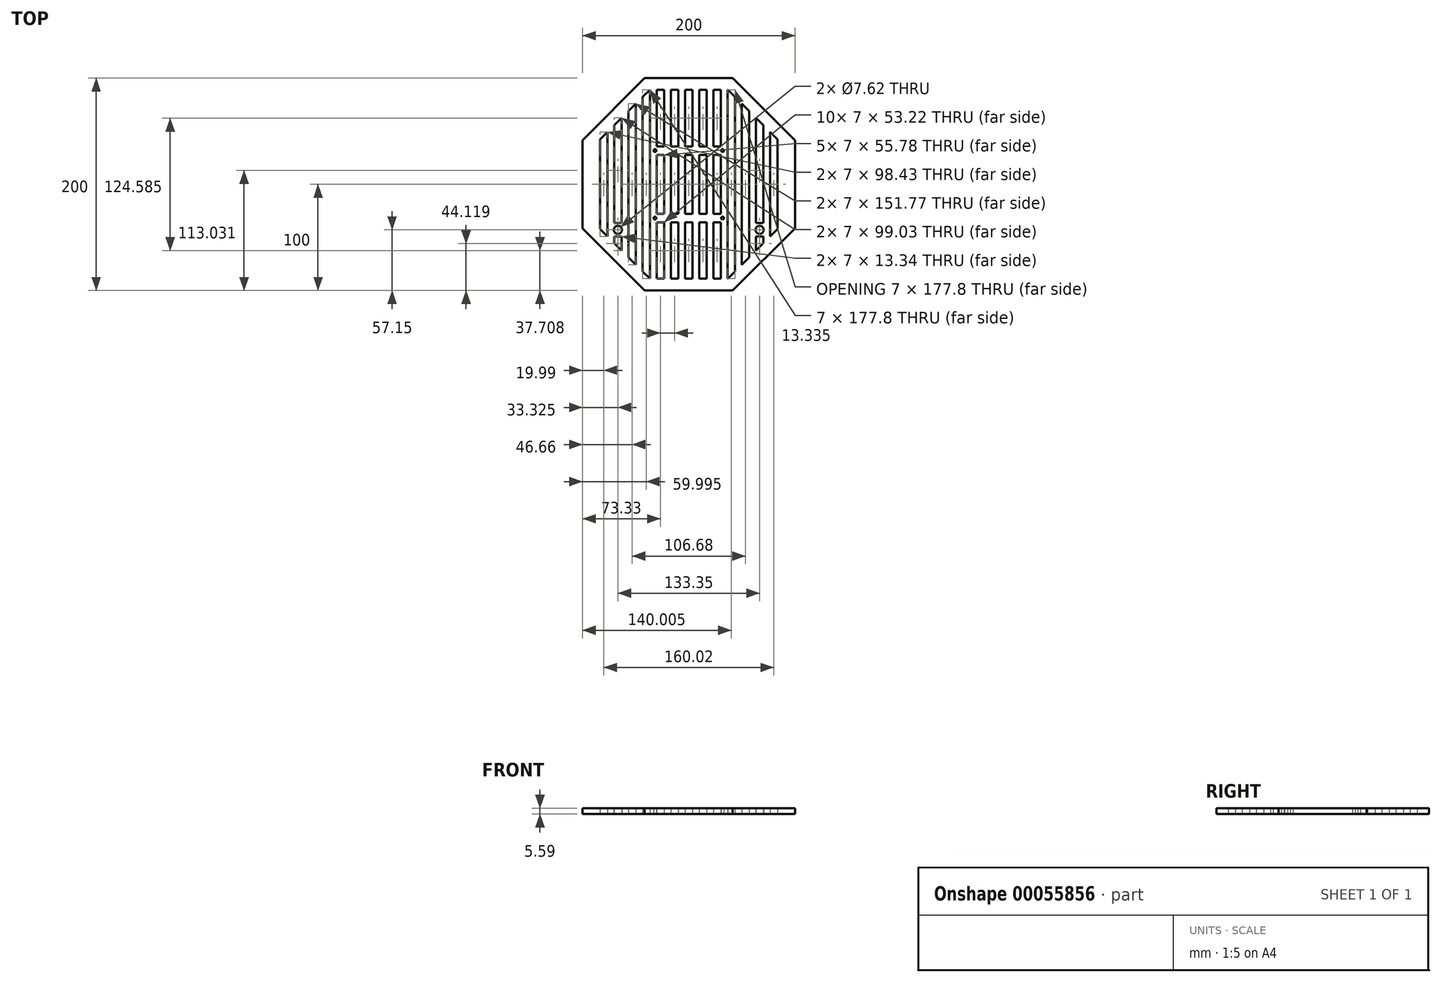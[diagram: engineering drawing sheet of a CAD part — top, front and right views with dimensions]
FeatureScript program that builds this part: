
annotation { "Feature Type Name" : "Feature", "Feature Type Description" : "" }
export const myFeature = defineFeature(function(context is Context, id is Id, definition is map)
    precondition{}
    {
        {
            var Q0;
            Q0=qCreatedBy(makeId("Top.planeOp"),FACE);
            var sketch = newSketch(context, id + "F0", { "sketchPlane" : qUnion([Q0])});
            skLineSegment(sketch, "E0.0", {"start": v(-41.42, 100) * mm, "end": v(41.42, 100) * mm});
            skLineSegment(sketch, "E0.2", {"start": v(100, 41.42) * mm, "end": v(100, -41.42) * mm});
            skLineSegment(sketch, "E0.3", {"start": v(100, -41.42) * mm, "end": v(41.42, -100) * mm});
            skLineSegment(sketch, "E0.4", {"start": v(41.42, -100) * mm, "end": v(-41.42, -100) * mm});
            skLineSegment(sketch, "E0.5", {"start": v(-41.42, -100) * mm, "end": v(-100, -41.42) * mm});
            skLineSegment(sketch, "E0.6", {"start": v(-100, -41.42) * mm, "end": v(-100, 41.42) * mm});
            skLineSegment(sketch, "E0.7", {"start": v(-100, 41.42) * mm, "end": v(-41.42, 100) * mm});
            skPoint(sketch, "E0.0.midPoint", {"position": v(0, 100) * mm});
            skPoint(sketch, "E1.rect.middle", {"position": v(0, 0) * mm});
            skCircle(sketch, "E2", {"center": v(-31.79, 31.79) * mm, "radius": 1.3 * mm});
            skCircle(sketch, "E3", {"center": v(31.79, 31.79) * mm, "radius": 1.3 * mm});
            skCircle(sketch, "E4", {"center": v(-31.79, -31.79) * mm, "radius": 1.3 * mm});
            skCircle(sketch, "E5", {"center": v(31.79, -31.79) * mm, "radius": 1.3 * mm});
            skPoint(sketch, "E6", {"position": v(0, -42.85) * mm});
            skCircle(sketch, "E7", {"center": v(-66.68, -42.85) * mm, "radius": 3.81 * mm});
            skCircle(sketch, "E8", {"center": v(66.68, -42.85) * mm, "radius": 3.81 * mm});
            skPoint(sketch, "E9.0.midPoint", {"position": v(0, 88.9) * mm});
            skLineSegment(sketch, "E10.bottom", {"start": v(-3.5, 88.9) * mm, "end": v(3.5, 88.9) * mm});
            skLineSegment(sketch, "E10.top", {"start": v(-3.5, -88.9) * mm, "end": v(3.5, -88.9) * mm});
            skLineSegment(sketch, "E10.left", {"start": v(-3.5, 88.9) * mm, "end": v(-3.5, 35.68) * mm});
            skLineSegment(sketch, "E10.right", {"start": v(3.5, 88.9) * mm, "end": v(3.5, 35.68) * mm});
            skLineSegment(sketch, "E11.1.0.0", {"start": v(9.84, 88.9) * mm, "end": v(9.84, 35.68) * mm});
            skLineSegment(sketch, "E11.1.0.1", {"start": v(16.84, 88.9) * mm, "end": v(16.84, 35.68) * mm});
            skPoint(sketch, "E11.1.0.2", {"position": v(13.33, -42.85) * mm});
            skPoint(sketch, "E11.1.0.3", {"position": v(13.33, 0) * mm});
            skPoint(sketch, "E11.1.0.4", {"position": v(13.33, 88.9) * mm});
            skPoint(sketch, "E11.1.0.5", {"position": v(13.33, 0) * mm});
            skLineSegment(sketch, "E11.1.0.6", {"start": v(9.84, 88.9) * mm, "end": v(16.84, 88.9) * mm});
            skLineSegment(sketch, "E11.1.0.7", {"start": v(9.84, -88.9) * mm, "end": v(16.84, -88.9) * mm});
            skLineSegment(sketch, "E11.2.0.0", {"start": v(23.17, 88.9) * mm, "end": v(23.17, 35.68) * mm});
            skLineSegment(sketch, "E11.2.0.1", {"start": v(30.17, 88.9) * mm, "end": v(30.17, 35.68) * mm});
            skPoint(sketch, "E11.2.0.2", {"position": v(26.67, -42.85) * mm});
            skPoint(sketch, "E11.2.0.3", {"position": v(26.67, 0) * mm});
            skPoint(sketch, "E11.2.0.4", {"position": v(26.67, 88.9) * mm});
            skPoint(sketch, "E11.2.0.5", {"position": v(26.67, 0) * mm});
            skLineSegment(sketch, "E11.2.0.6", {"start": v(23.17, 88.9) * mm, "end": v(30.17, 88.9) * mm});
            skLineSegment(sketch, "E11.2.0.7", {"start": v(23.17, -88.9) * mm, "end": v(30.17, -88.9) * mm});
            skLineSegment(sketch, "E11.3.0.0", {"start": v(36.5, 88.9) * mm, "end": v(36.5, -88.9) * mm});
            skLineSegment(sketch, "E11.3.0.1", {"start": v(43.5, 82.22) * mm, "end": v(43.5, -82.22) * mm});
            skPoint(sketch, "E11.3.0.2", {"position": v(40, -42.85) * mm});
            skPoint(sketch, "E11.3.0.3", {"position": v(40, 0) * mm});
            skPoint(sketch, "E11.3.0.5", {"position": v(40, 0) * mm});
            skLineSegment(sketch, "E11.3.0.6", {"start": v(36.5, 88.9) * mm, "end": v(36.82, 88.9) * mm});
            skLineSegment(sketch, "E11.3.0.7", {"start": v(36.5, -88.9) * mm, "end": v(36.82, -88.9) * mm});
            skPoint(sketch, "E11.4.0.2", {"position": v(53.34, -42.85) * mm});
            skPoint(sketch, "E11.4.0.3", {"position": v(53.34, 0) * mm});
            skPoint(sketch, "E11.4.0.5", {"position": v(53.34, 0) * mm});
            skPoint(sketch, "E11.5.0.2", {"position": v(66.67, -42.85) * mm});
            skPoint(sketch, "E11.5.0.3", {"position": v(66.67, 0) * mm});
            skPoint(sketch, "E11.5.0.5", {"position": v(66.67, 0) * mm});
            skLineSegment(sketch, "E11.6.0.1", {"start": v(83.51, 42.21) * mm, "end": v(83.51, -42.21) * mm});
            skPoint(sketch, "E11.6.0.2", {"position": v(80, -42.85) * mm});
            skPoint(sketch, "E11.6.0.3", {"position": v(80, 0) * mm});
            skPoint(sketch, "E11.6.0.5", {"position": v(80, 0) * mm});
            skLineSegment(sketch, "E11.direction1", {"start": v(-3.5, -88.9) * mm, "end": v(9.84, -88.9) * mm, "construction": true});
            skLineSegment(sketch, "E12", {"start": v(0, 88.9) * mm, "end": v(0, -110.43) * mm, "construction": true});
            skPoint(sketch, "E12.endSnap0", {"position": v(0, -100) * mm});
            skLineSegment(sketch, "E13.MirrorCS", {"start": v(-36.5, 88.9) * mm, "end": v(-36.82, 88.9) * mm});
            skLineSegment(sketch, "E14.MirrorCS", {"start": v(-9.84, 88.9) * mm, "end": v(-16.84, 88.9) * mm});
            skLineSegment(sketch, "E15.MirrorCS", {"start": v(-23.17, -88.9) * mm, "end": v(-30.17, -88.9) * mm});
            skLineSegment(sketch, "E16.MirrorCS", {"start": v(-23.17, 88.9) * mm, "end": v(-30.17, 88.9) * mm});
            skLineSegment(sketch, "E17.MirrorCS", {"start": v(-36.5, -88.9) * mm, "end": v(-36.82, -88.9) * mm});
            skLineSegment(sketch, "E18.MirrorCS", {"start": v(-9.83, -88.9) * mm, "end": v(-16.83, -88.9) * mm});
            skPoint(sketch, "E19.MirrorP", {"position": v(-66.67, 0) * mm});
            skPoint(sketch, "E20.MirrorP", {"position": v(-53.34, 0) * mm});
            skPoint(sketch, "E21.MirrorP", {"position": v(-40, 0) * mm});
            skPoint(sketch, "E22.MirrorP", {"position": v(-26.67, 0) * mm});
            skPoint(sketch, "E23.MirrorP", {"position": v(-13.33, 0) * mm});
            skArc(sketch, "E24.MirrorC", {"start": v(-63.17, -44.36) * mm, "mid": v(-70.48, -42.85) * mm, "end": v(-63.17, -41.34) * mm});
            skPoint(sketch, "E25.MirrorP", {"position": v(-80, 0) * mm});
            skLineSegment(sketch, "E26.MirrorCS", {"start": v(-30.17, 88.9) * mm, "end": v(-30.17, 35.68) * mm});
            skPoint(sketch, "E27.MirrorP", {"position": v(-26.67, -42.85) * mm});
            skPoint(sketch, "E28.MirrorP", {"position": v(-40, -42.85) * mm});
            skLineSegment(sketch, "E29.MirrorCS", {"start": v(-16.84, 88.9) * mm, "end": v(-16.83, 35.68) * mm});
            skPoint(sketch, "E30.MirrorP", {"position": v(-53.34, -42.85) * mm});
            skPoint(sketch, "E31.MirrorP", {"position": v(-13.33, 88.9) * mm});
            skLineSegment(sketch, "E32.MirrorCS", {"start": v(-36.5, 88.9) * mm, "end": v(-36.5, -88.9) * mm});
            skLineSegment(sketch, "E33.MirrorCS", {"start": v(-43.5, 82.22) * mm, "end": v(-43.5, -82.22) * mm});
            skPoint(sketch, "E34.MirrorP", {"position": v(-13.33, -42.85) * mm});
            skLineSegment(sketch, "E35.MirrorCS", {"start": v(-9.84, 88.9) * mm, "end": v(-9.83, 35.68) * mm});
            skPoint(sketch, "E36.MirrorP", {"position": v(-66.67, -42.85) * mm});
            skPoint(sketch, "E37.MirrorP", {"position": v(-26.67, 88.9) * mm});
            skLineSegment(sketch, "E38.MirrorCS", {"start": v(-23.17, 88.9) * mm, "end": v(-23.17, 35.68) * mm});
            skPoint(sketch, "E39.MirrorP", {"position": v(-80, -42.85) * mm});
            skLineSegment(sketch, "E40.trimOffspring", {"start": v(-83.5, 42.21) * mm, "end": v(-83.5, -42.21) * mm});
            skLineSegment(sketch, "E41.trimOffspring", {"start": v(-76.5, 49.21) * mm, "end": v(-76.5, -49.21) * mm});
            skLineSegment(sketch, "E42.trimOffspring", {"start": v(-70.17, 55.55) * mm, "end": v(-70.17, -36.49) * mm});
            skLineSegment(sketch, "E43.trimOffspring", {"start": v(-63.17, 62.55) * mm, "end": v(-63.17, -36.49) * mm});
            skLineSegment(sketch, "E44.trimOffspring", {"start": v(-56.84, 68.88) * mm, "end": v(-56.84, -68.88) * mm});
            skLineSegment(sketch, "E45.trimOffspring", {"start": v(-49.84, 75.88) * mm, "end": v(-49.84, -75.88) * mm});
            skLineSegment(sketch, "E46.trimOffspring", {"start": v(49.84, 75.88) * mm, "end": v(49.84, -75.88) * mm});
            skLineSegment(sketch, "E47.trimOffspring", {"start": v(56.84, 68.88) * mm, "end": v(56.84, -68.88) * mm});
            skLineSegment(sketch, "E48.trimOffspring", {"start": v(63.17, 62.55) * mm, "end": v(63.17, -36.49) * mm});
            skLineSegment(sketch, "E49.trimOffspring", {"start": v(76.5, 49.21) * mm, "end": v(76.5, -49.21) * mm});
            skLineSegment(sketch, "E50", {"start": v(41.42, 100) * mm, "end": v(100, 41.42) * mm});
            skLineSegment(sketch, "E51", {"start": v(-36.5, -88.9) * mm, "end": v(-43.5, -82.22) * mm});
            skLineSegment(sketch, "E52", {"start": v(-49.84, -75.88) * mm, "end": v(-56.84, -68.88) * mm});
            skLineSegment(sketch, "E53", {"start": v(-63.17, -62.55) * mm, "end": v(-70.17, -55.55) * mm});
            skLineSegment(sketch, "E54", {"start": v(-76.5, -49.21) * mm, "end": v(-83.5, -42.21) * mm});
            skLineSegment(sketch, "E55", {"start": v(36.82, -88.9) * mm, "end": v(43.5, -82.22) * mm});
            skLineSegment(sketch, "E56", {"start": v(49.84, -75.88) * mm, "end": v(56.84, -68.88) * mm});
            skLineSegment(sketch, "E57", {"start": v(63.17, -62.55) * mm, "end": v(70.17, -55.55) * mm});
            skLineSegment(sketch, "E58", {"start": v(76.5, -49.21) * mm, "end": v(83.51, -42.21) * mm});
            skLineSegment(sketch, "E59", {"start": v(83.51, 42.21) * mm, "end": v(76.5, 49.21) * mm});
            skLineSegment(sketch, "E60", {"start": v(70.17, 55.55) * mm, "end": v(63.17, 62.55) * mm});
            skLineSegment(sketch, "E61", {"start": v(56.84, 68.88) * mm, "end": v(49.84, 75.88) * mm});
            skLineSegment(sketch, "E62", {"start": v(43.5, 82.22) * mm, "end": v(36.82, 88.9) * mm});
            skLineSegment(sketch, "E63", {"start": v(-36.5, 88.9) * mm, "end": v(-43.5, 82.22) * mm});
            skLineSegment(sketch, "E64", {"start": v(-49.84, 75.88) * mm, "end": v(-56.84, 68.88) * mm});
            skLineSegment(sketch, "E65", {"start": v(-63.17, 62.55) * mm, "end": v(-70.17, 55.55) * mm});
            skLineSegment(sketch, "E66", {"start": v(-76.5, 49.21) * mm, "end": v(-83.5, 42.21) * mm});
            skLineSegment(sketch, "E67.left", {"start": v(-76.5, -49.21) * mm, "end": v(-76.5, -36.49) * mm});
            skLineSegment(sketch, "E67.right", {"start": v(-56.84, -49.21) * mm, "end": v(-56.84, -36.49) * mm});
            skLineSegment(sketch, "E68.left", {"start": v(76.5, -49.21) * mm, "end": v(76.5, -36.49) * mm});
            skLineSegment(sketch, "E68.right", {"start": v(56.84, -49.21) * mm, "end": v(56.84, -36.49) * mm});
            skLineSegment(sketch, "E69.trimOffspring", {"start": v(-70.17, -49.21) * mm, "end": v(-70.17, -55.55) * mm});
            skLineSegment(sketch, "E70.trimOffspring", {"start": v(-63.17, -49.21) * mm, "end": v(-63.17, -62.55) * mm});
            skLineSegment(sketch, "E71.trimOffspring", {"start": v(63.17, -49.21) * mm, "end": v(63.17, -62.55) * mm});
            skLineSegment(sketch, "E72.trimOffspring", {"start": v(70.17, -49.21) * mm, "end": v(70.17, -55.55) * mm});
            skLineSegment(sketch, "E73", {"start": v(70.17, -36.49) * mm, "end": v(70.17, 55.55) * mm});
            skLineSegment(sketch, "E74", {"start": v(-70.17, -36.49) * mm, "end": v(-63.17, -36.49) * mm});
            skLineSegment(sketch, "E75", {"start": v(-70.17, -49.21) * mm, "end": v(-63.17, -49.21) * mm});
            skLineSegment(sketch, "E76", {"start": v(63.17, -36.49) * mm, "end": v(70.17, -36.49) * mm});
            skLineSegment(sketch, "E77", {"start": v(63.17, -49.21) * mm, "end": v(70.17, -49.21) * mm});
            skLineSegment(sketch, "E78.bottom", {"start": v(30.17, -35.68) * mm, "end": v(23.17, -35.68) * mm});
            skLineSegment(sketch, "E78.top", {"start": v(30.17, -27.9) * mm, "end": v(23.17, -27.9) * mm});
            skLineSegment(sketch, "E78.left", {"start": v(36.5, -35.68) * mm, "end": v(36.5, -27.9) * mm});
            skLineSegment(sketch, "E78.right", {"start": v(-36.5, -35.68) * mm, "end": v(-36.5, -27.9) * mm});
            skPoint(sketch, "E78.middle", {"position": v(0, -31.79) * mm});
            skLineSegment(sketch, "E79", {"start": v(0, 0) * mm, "end": v(-34.12, 0) * mm, "construction": true});
            skPoint(sketch, "E79.endSnap0", {"position": v(-30.17, 0) * mm});
            skLineSegment(sketch, "E80.MirrorCS", {"start": v(30.17, 27.9) * mm, "end": v(23.17, 27.9) * mm});
            skLineSegment(sketch, "E81.MirrorCS", {"start": v(30.17, 35.68) * mm, "end": v(23.17, 35.68) * mm});
            skLineSegment(sketch, "E82", {"start": v(-36.5, 27.9) * mm, "end": v(-36.5, 35.68) * mm});
            skLineSegment(sketch, "E83", {"start": v(36.5, 27.9) * mm, "end": v(36.5, 35.68) * mm});
            skLineSegment(sketch, "E84.trimOffspring", {"start": v(-23.17, 27.9) * mm, "end": v(-30.17, 27.9) * mm});
            skLineSegment(sketch, "E85.trimOffspring", {"start": v(-9.83, 27.9) * mm, "end": v(-16.83, 27.9) * mm});
            skLineSegment(sketch, "E86.trimOffspring", {"start": v(3.5, 27.9) * mm, "end": v(-3.5, 27.9) * mm});
            skLineSegment(sketch, "E87.trimOffspring", {"start": v(16.84, 27.9) * mm, "end": v(9.84, 27.9) * mm});
            skLineSegment(sketch, "E88.trimOffspring", {"start": v(-23.17, 35.68) * mm, "end": v(-30.17, 35.68) * mm});
            skLineSegment(sketch, "E89.trimOffspring", {"start": v(-9.83, 35.68) * mm, "end": v(-16.83, 35.68) * mm});
            skLineSegment(sketch, "E90.trimOffspring", {"start": v(3.5, 35.68) * mm, "end": v(-3.5, 35.68) * mm});
            skLineSegment(sketch, "E91.trimOffspring", {"start": v(16.84, 35.68) * mm, "end": v(9.83, 35.68) * mm});
            skLineSegment(sketch, "E92.trimOffspring", {"start": v(-30.17, 27.9) * mm, "end": v(-30.17, -27.9) * mm});
            skLineSegment(sketch, "E93.trimOffspring", {"start": v(-23.17, 27.9) * mm, "end": v(-23.17, -27.9) * mm});
            skLineSegment(sketch, "E94.trimOffspring", {"start": v(-16.83, 27.9) * mm, "end": v(-16.83, -27.9) * mm});
            skLineSegment(sketch, "E95.trimOffspring", {"start": v(-9.83, 27.9) * mm, "end": v(-9.83, -27.9) * mm});
            skLineSegment(sketch, "E96.trimOffspring", {"start": v(-3.5, 27.9) * mm, "end": v(-3.5, -27.9) * mm});
            skLineSegment(sketch, "E97.trimOffspring", {"start": v(3.5, 27.9) * mm, "end": v(3.5, -27.9) * mm});
            skLineSegment(sketch, "E98.trimOffspring", {"start": v(9.84, 27.9) * mm, "end": v(9.84, -27.9) * mm});
            skLineSegment(sketch, "E99.trimOffspring", {"start": v(16.84, 27.9) * mm, "end": v(16.84, -27.9) * mm});
            skLineSegment(sketch, "E100.trimOffspring", {"start": v(23.17, 27.9) * mm, "end": v(23.17, -27.9) * mm});
            skLineSegment(sketch, "E101.trimOffspring", {"start": v(30.17, 27.9) * mm, "end": v(30.17, -27.9) * mm});
            skLineSegment(sketch, "E102.trimOffspring", {"start": v(-23.17, -27.9) * mm, "end": v(-30.17, -27.9) * mm});
            skLineSegment(sketch, "E103.trimOffspring", {"start": v(-9.83, -27.9) * mm, "end": v(-16.83, -27.9) * mm});
            skLineSegment(sketch, "E104.trimOffspring", {"start": v(3.5, -27.9) * mm, "end": v(-3.5, -27.9) * mm});
            skLineSegment(sketch, "E105.trimOffspring", {"start": v(16.84, -27.9) * mm, "end": v(9.84, -27.9) * mm});
            skLineSegment(sketch, "E106.trimOffspring", {"start": v(3.5, -35.68) * mm, "end": v(-3.5, -35.68) * mm});
            skLineSegment(sketch, "E107.trimOffspring", {"start": v(-9.83, -35.68) * mm, "end": v(-16.83, -35.68) * mm});
            skLineSegment(sketch, "E108.trimOffspring", {"start": v(-23.17, -35.68) * mm, "end": v(-30.17, -35.68) * mm});
            skLineSegment(sketch, "E109.trimOffspring", {"start": v(-30.17, -35.68) * mm, "end": v(-30.17, -88.9) * mm});
            skLineSegment(sketch, "E110.trimOffspring", {"start": v(-23.17, -35.68) * mm, "end": v(-23.17, -88.9) * mm});
            skLineSegment(sketch, "E111.trimOffspring", {"start": v(-16.83, -35.68) * mm, "end": v(-16.83, -88.9) * mm});
            skLineSegment(sketch, "E112.trimOffspring", {"start": v(-9.83, -35.68) * mm, "end": v(-9.83, -88.9) * mm});
            skLineSegment(sketch, "E113.trimOffspring", {"start": v(-3.5, -35.68) * mm, "end": v(-3.5, -88.9) * mm});
            skLineSegment(sketch, "E114.trimOffspring", {"start": v(3.5, -35.68) * mm, "end": v(3.5, -88.9) * mm});
            skLineSegment(sketch, "E115.trimOffspring", {"start": v(23.17, -35.68) * mm, "end": v(23.17, -88.9) * mm});
            skLineSegment(sketch, "E116.trimOffspring", {"start": v(30.17, -35.68) * mm, "end": v(30.17, -88.9) * mm});
            skLineSegment(sketch, "E117", {"start": v(9.84, -35.68) * mm, "end": v(16.84, -35.68) * mm});
            skLineSegment(sketch, "E118.trimOffspring", {"start": v(9.84, -35.68) * mm, "end": v(9.84, -88.9) * mm});
            skLineSegment(sketch, "E119.trimOffspring", {"start": v(16.84, -35.68) * mm, "end": v(16.84, -88.9) * mm});
            skSolve(sketch);
        }
        {
            var Q0;
            Q0=qSketchRegion(id+"F0",true);
            extrude(context, id + "F1", {"entities" : qUnion([Q0]), "depth" : 5.6 * mm});
        }
    });
